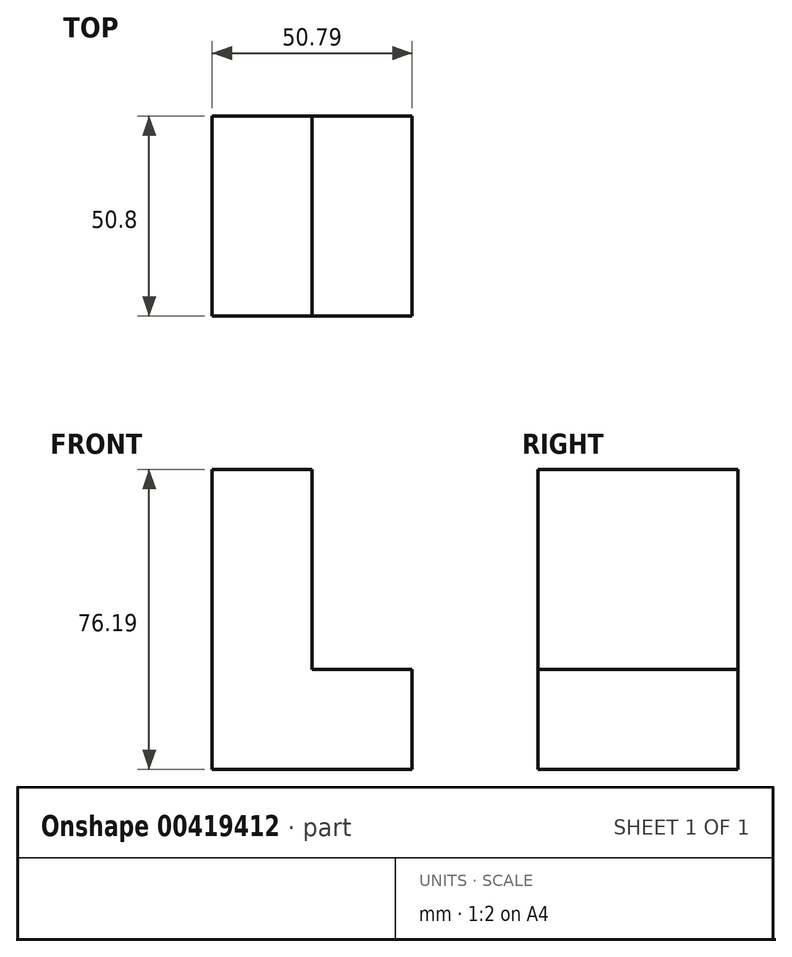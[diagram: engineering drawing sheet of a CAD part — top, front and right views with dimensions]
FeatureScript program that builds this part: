
annotation { "Feature Type Name" : "Feature", "Feature Type Description" : "" }
export const myFeature = defineFeature(function(context is Context, id is Id, definition is map)
    precondition{}
    {
        {
            var Q0;
            Q0=qCreatedBy(makeId("Front.planeOp"),FACE);
            var sketch = newSketch(context, id + "F0", { "sketchPlane" : qUnion([Q0])});
            skLineSegment(sketch, "E0", {"start": v(-74.1, 50.8) * mm, "end": v(-48.7, 50.8) * mm});
            skLineSegment(sketch, "E1", {"start": v(-48.7, 50.8) * mm, "end": v(-48.7, 0) * mm});
            skLineSegment(sketch, "E2", {"start": v(-48.7, 0) * mm, "end": v(-23.3, 0) * mm});
            skLineSegment(sketch, "E3", {"start": v(-23.3, 0) * mm, "end": v(-23.3, -25.4) * mm});
            skLineSegment(sketch, "E4", {"start": v(-74.1, 50.8) * mm, "end": v(-74.1, -25.4) * mm});
            skLineSegment(sketch, "E5", {"start": v(-74.1, -25.4) * mm, "end": v(-23.3, -25.4) * mm});
            skSolve(sketch);
        }
        {
            var Q0;
            Q0=makeQuery(id+"F0.imprint","IMPRINT",FACE,{"disambiguationData":[TD([[makeQuery(id+"F0.imprint","IMPRINT",EDGE,{"derivedFrom":sQuery(id+"F0.wireOp",EDGE,"E0")}),-1.0]])]});
            extrude(context, id + "F1", {"entities" : qUnion([Q0]), "depth" : 50.8 * mm});
        }
    });
